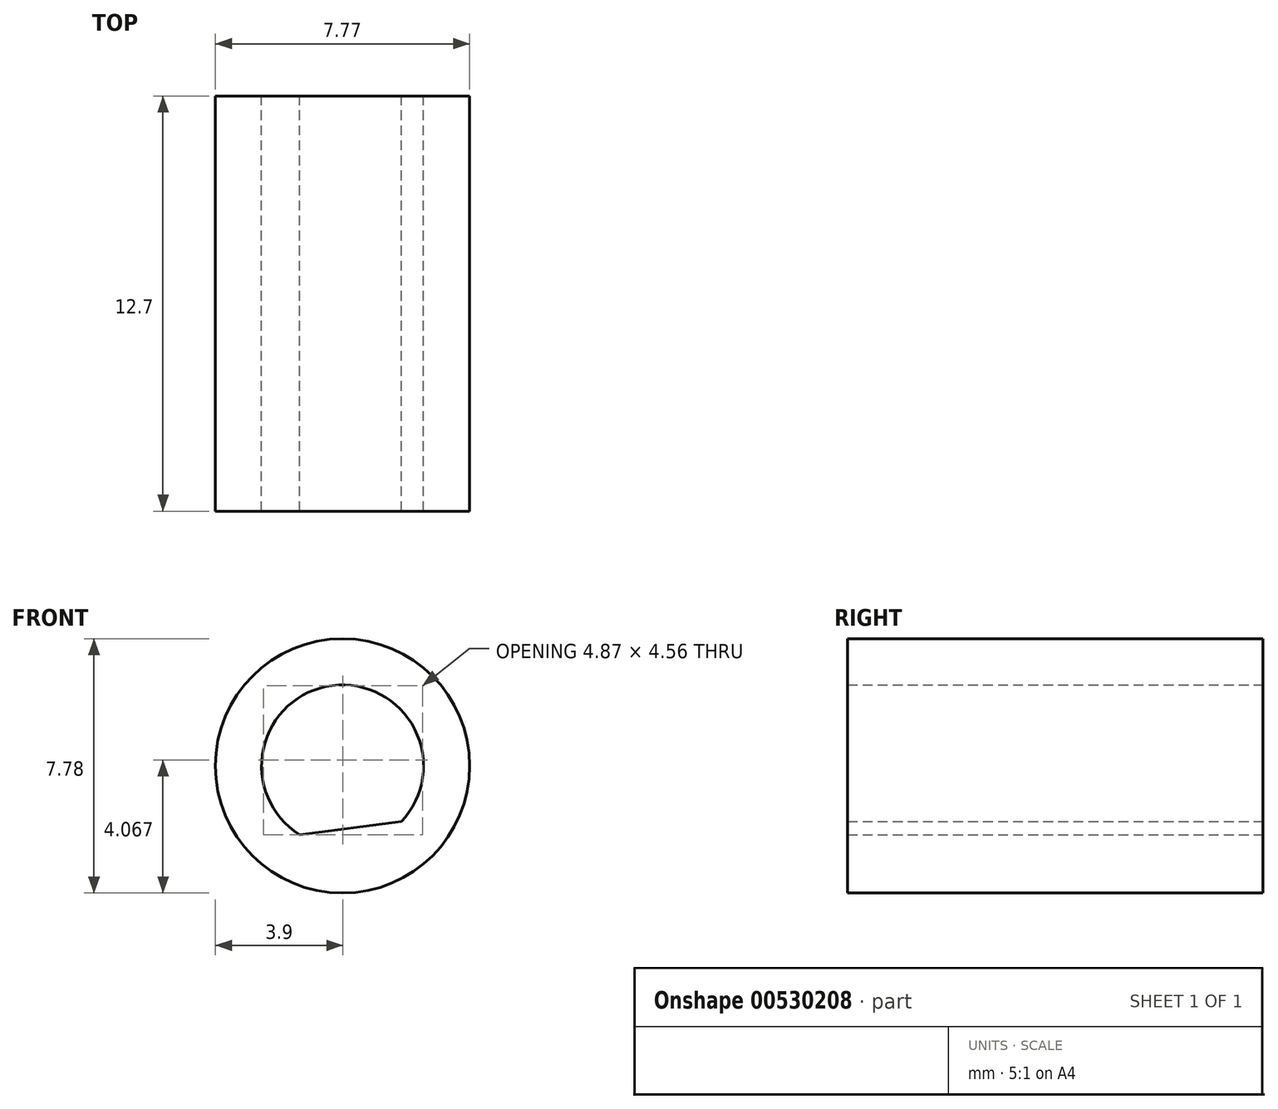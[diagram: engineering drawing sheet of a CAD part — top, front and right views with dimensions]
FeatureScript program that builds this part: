
annotation { "Feature Type Name" : "Feature", "Feature Type Description" : "" }
export const myFeature = defineFeature(function(context is Context, id is Id, definition is map)
    precondition{}
    {
        {
            var Q0;
            Q0=qCreatedBy(makeId("Front.planeOp"),FACE);
            var sketch = newSketch(context, id + "F0", { "sketchPlane" : qUnion([Q0])});
            skCircle(sketch, "E0", {"center": v(-39.99, 31.33) * mm, "radius": 3.89 * mm});
            skCircle(sketch, "E1", {"center": v(-39.99, 31.33) * mm, "radius": 2.48 * mm});
            skLineSegment(sketch, "E2", {"start": v(-41.3, 29.23) * mm, "end": v(-38.19, 29.63) * mm});
            skSolve(sketch);
        }
        {
            var Q0;
            Q0=makeQuery(id+"F0.imprint","IMPRINT",FACE,{"disambiguationData":[TD([[makeQuery(id+"F0.imprint","IMPRINT",EDGE,{"derivedFrom":sQuery(id+"F0.wireOp",EDGE,"E0")}),1.0]])]});
            var Q1;
            {var subQ0=sQuery(id+"F0.wireOp",EDGE,"E2");Q1=makeQuery(id+"F0.imprint","IMPRINT",FACE,{"disambiguationData":[TD([[makeQuery(id+"F0.imprint","IMPRINT",EDGE,{"derivedFrom":subQ0}),-1.0]])]});}
            extrude(context, id + "F1", {"entities" : qUnion([Q0, Q1]), "depth" : 12.7 * mm, "offsetDistance" : 25.4 * mm});
        }
    });
